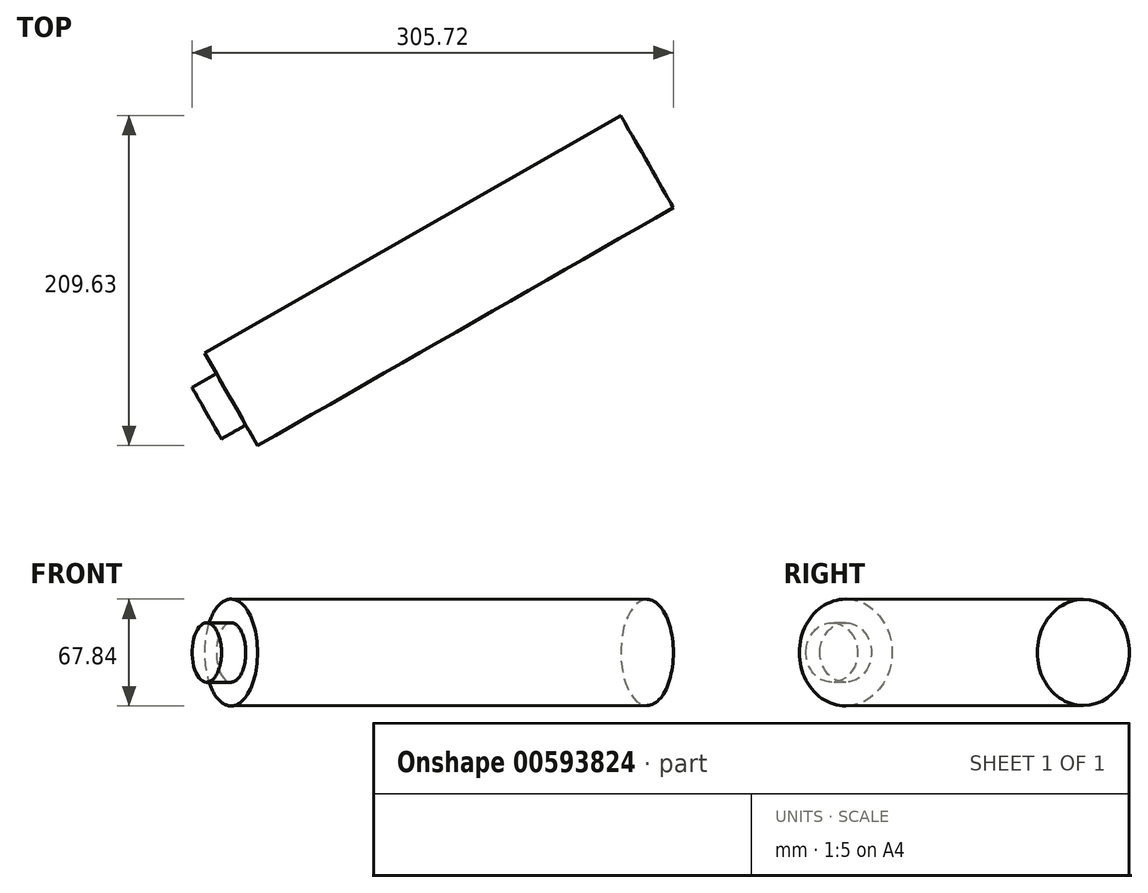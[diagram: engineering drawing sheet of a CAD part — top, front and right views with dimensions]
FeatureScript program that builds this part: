
annotation { "Feature Type Name" : "Feature", "Feature Type Description" : "" }
export const myFeature = defineFeature(function(context is Context, id is Id, definition is map)
    precondition{}
    {
        {
            var Q0;
            Q0=qCreatedBy(makeId("Top.planeOp"),FACE);
            var sketch = newSketch(context, id + "F0", { "sketchPlane" : qUnion([Q0])});
            skLineSegment(sketch, "E0", {"start": v(-133.15, -57.94) * mm, "end": v(146.3, 101.66) * mm});
            skLineSegment(sketch, "E1", {"start": v(146.3, 101.66) * mm, "end": v(129.58, 130.92) * mm});
            skLineSegment(sketch, "E2", {"start": v(129.58, 130.92) * mm, "end": v(-134.76, -19.8) * mm});
            skLineSegment(sketch, "E3", {"start": v(-134.76, -19.8) * mm, "end": v(-127.3, -32.9) * mm});
            skLineSegment(sketch, "E4", {"start": v(-127.3, -32.9) * mm, "end": v(-142.72, -41.7) * mm});
            skLineSegment(sketch, "E5", {"start": v(-142.72, -41.7) * mm, "end": v(-133.15, -57.94) * mm});
            skSolve(sketch);
        }
        {
            var Q0;
            Q0 = qSketchRegion(id + "F0", true);
            var Q1;
            Q1=sQuery(id+"F0.wireOp",EDGE,"E0");
            revolve(context, id + "F1", {"entities" : qUnion([Q0]), "axis" : qUnion([Q1]), "revolveType" : RevolveType.FULL});
        }
    });
